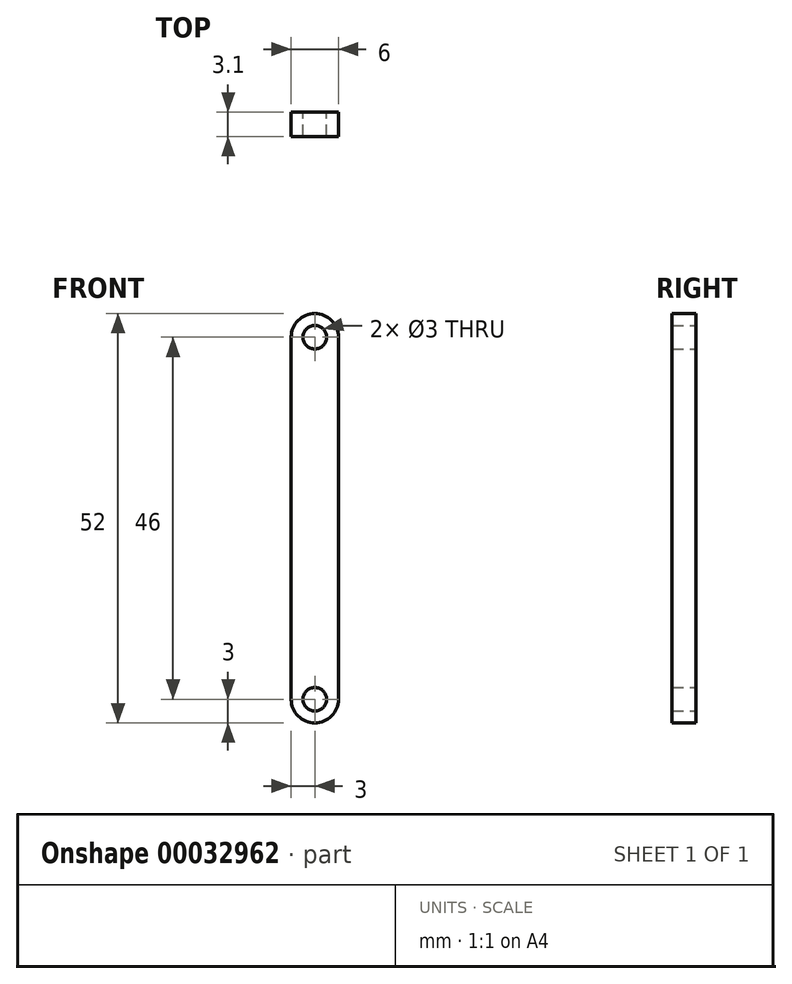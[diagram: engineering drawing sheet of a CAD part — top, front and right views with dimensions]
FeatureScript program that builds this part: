
annotation { "Feature Type Name" : "Feature", "Feature Type Description" : "" }
export const myFeature = defineFeature(function(context is Context, id is Id, definition is map)
    precondition{}
    {
        {
            var Q0;
            Q0=qCreatedBy(makeId("Front.planeOp"),FACE);
            var sketch = newSketch(context, id + "F0", { "sketchPlane" : qUnion([Q0])});
            skCircle(sketch, "E0", {"center": v(0, 23) * mm, "radius": 1.5 * mm});
            skArc(sketch, "E1.0", {"start": v(3, 23) * mm, "mid": v(0, 26) * mm, "end": v(-3, 23) * mm});
            skLineSegment(sketch, "E2", {"start": v(-3, 23) * mm, "end": v(3, 23) * mm, "construction": true});
            skLineSegment(sketch, "E3", {"start": v(-3, 23) * mm, "end": v(-3, 0) * mm});
            skLineSegment(sketch, "E4.MirrorCS", {"start": v(3, 23) * mm, "end": v(3, 0) * mm});
            skLineSegment(sketch, "E5.MirrorCS", {"start": v(3, -23) * mm, "end": v(3, 0) * mm});
            skLineSegment(sketch, "E6.MirrorCS", {"start": v(-3, -23) * mm, "end": v(-3, 0) * mm});
            skArc(sketch, "E7.MirrorCS", {"start": v(3, -23) * mm, "mid": v(0, -26) * mm, "end": v(-3, -23) * mm});
            skCircle(sketch, "E8.MirrorC", {"center": v(0, -23) * mm, "radius": 1.5 * mm});
            skSolve(sketch);
        }
        {
            var Q0;
            Q0 = qSketchRegion(id + "F0", true);
            extrude(context, id + "F1", {"entities" : qUnion([Q0]), "depth" : 3.1 * mm});
        }
    });
